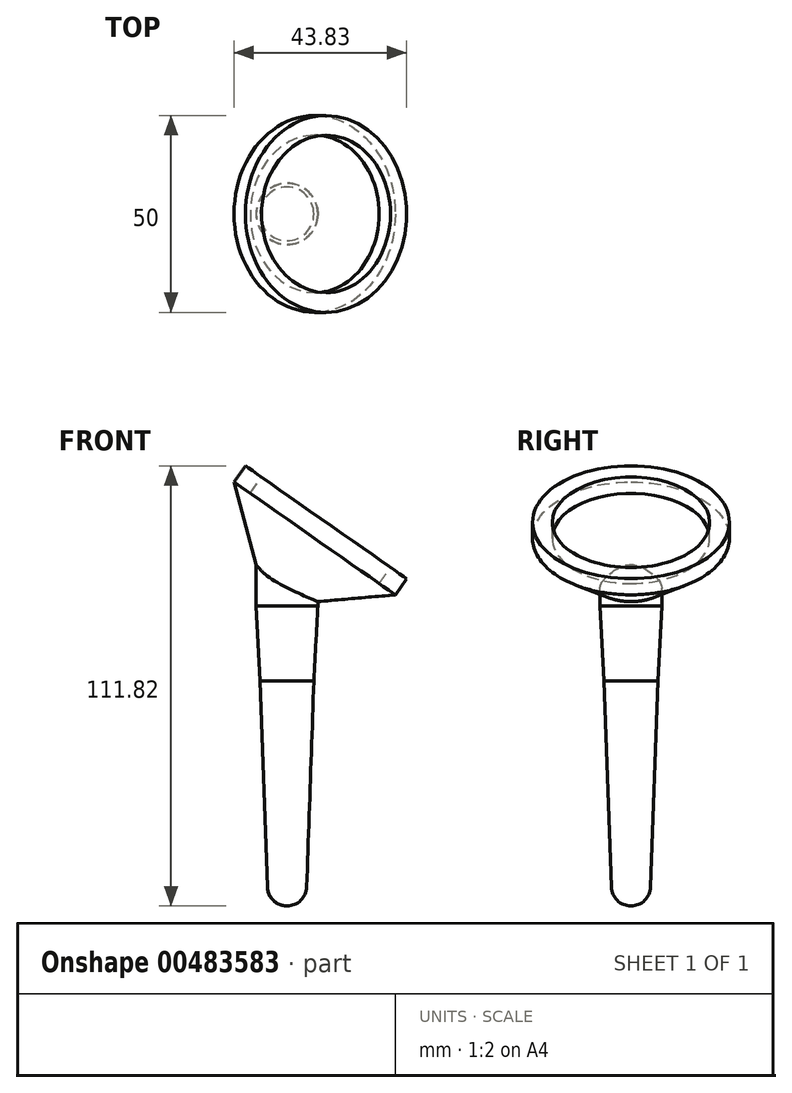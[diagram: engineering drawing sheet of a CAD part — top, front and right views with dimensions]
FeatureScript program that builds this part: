
annotation { "Feature Type Name" : "Feature", "Feature Type Description" : "" }
export const myFeature = defineFeature(function(context is Context, id is Id, definition is map)
    precondition{}
    {
        {
            var Q0;
            Q0=qCreatedBy(makeId("Front.planeOp"),FACE);
            var sketch = newSketch(context, id + "F0", { "sketchPlane" : qUnion([Q0])});
            skLineSegment(sketch, "E0", {"start": v(0, 84.87) * mm, "end": v(0, -76.2) * mm, "construction": true});
            skLineSegment(sketch, "E1", {"start": v(-7.82, 0) * mm, "end": v(0, 0) * mm, "construction": true});
            skCircle(sketch, "E2", {"center": v(0, -71.2) * mm, "radius": 5 * mm, "construction": true});
            skArc(sketch, "E3", {"start": v(-5, -71.37) * mm, "mid": v(-3.47, -74.8) * mm, "end": v(0, -76.2) * mm});
            skLineSegment(sketch, "E4", {"start": v(-5, -71.37) * mm, "end": v(-6.82, -19.05) * mm});
            skLineSegment(sketch, "E5", {"start": v(-6.82, -19.05) * mm, "end": v(-7.82, 0) * mm});
            skLineSegment(sketch, "E6", {"start": v(0, 0) * mm, "end": v(0, -76.2) * mm});
            skLineSegment(sketch, "E7", {"start": v(-7.82, 0) * mm, "end": v(-7.82, 20) * mm});
            skLineSegment(sketch, "E8", {"start": v(-7.82, 20) * mm, "end": v(0, 20) * mm});
            skLineSegment(sketch, "E9", {"start": v(0, 20) * mm, "end": v(0, 0) * mm});
            skSolve(sketch);
        }
        {
            var Q0;
            Q0 = qSketchRegion(id + "F0", true);
            var Q1;
            Q1=sQuery(id+"F0.wireOp",EDGE,"E0");
            revolve(context, id + "F1", {"entities" : qUnion([Q0]), "axis" : qUnion([Q1]), "revolveType" : RevolveType.FULL});
        }
        {
            var Q0;
            Q0=qCreatedBy(makeId("Top.planeOp"),FACE);
            var sketch = newSketch(context, id + "F2", { "sketchPlane" : qUnion([Q0])});
            skLineSegment(sketch, "E10", {"start": v(0, 0) * mm, "end": v(0, -167.53) * mm, "construction": true});
            skSolve(sketch);
        }
        {
            var Q0;
            Q0=qCreatedBy(makeId("Front.planeOp"),FACE);
            var sketch = newSketch(context, id + "F3", { "sketchPlane" : qUnion([Q0])});
            skLineSegment(sketch, "E11", {"start": v(-5, 0) * mm, "end": v(9.9, 21.28) * mm, "construction": true});
            skLineSegment(sketch, "E12", {"start": v(-5, 0) * mm, "end": v(-5, 23.33) * mm, "construction": true});
            skLineSegment(sketch, "E13", {"start": v(-5, 0) * mm, "end": v(27.51, 2.84) * mm});
            skLineSegment(sketch, "E14", {"start": v(27.51, 2.84) * mm, "end": v(30.38, 6.94) * mm});
            skLineSegment(sketch, "E15", {"start": v(30.38, 6.94) * mm, "end": v(9.9, 21.28) * mm});
            skLineSegment(sketch, "E16", {"start": v(-5, 0) * mm, "end": v(9.9, 21.28) * mm});
            skLineSegment(sketch, "E17", {"start": v(0, 0) * mm, "end": v(-5, 0) * mm});
            skSolve(sketch);
        }
        {
            var Q0;
            Q0=makeQuery(id+"F3.imprint","IMPRINT",FACE,{"disambiguationData":[TD([[makeQuery(id+"F3.imprint","IMPRINT",EDGE,{"derivedFrom":sQuery(id+"F3.wireOp",EDGE,"E13")}),1.0]])]});
            var Q1;
            Q1=sQuery(id+"F3.wireOp",EDGE,"E16");
            revolve(context, id + "F4", {"operationType" : NewBodyOperationType.ADD, "entities" : qUnion([Q0]), "axis" : qUnion([Q1]), "revolveType" : RevolveType.FULL});
        }
        {
            var Q0;
            Q0=makeQuery(id+"F4.opRevolve","SWEPT_FACE",FACE,{"disambiguationData":[OSD([sQuery(id+"F3.wireOp",EDGE,"E15")])]});
            var sketch = newSketch(context, id + "F5", { "sketchPlane" : qUnion([Q0])});
            skCircle(sketch, "E18", {"center": v(-4.1, 0) * mm, "radius": 20 * mm});
            skSolve(sketch);
        }
        {
            var Q0;
            Q0=makeQuery(id+"F5.imprint","IMPRINT",FACE,{"disambiguationData":[TD([[makeQuery(id+"F5.imprint","IMPRINT",EDGE,{"derivedFrom":sQuery(id+"F5.wireOp",EDGE,"E18")}),1.0]])]});
            extrude(context, id + "F6", {"entities" : qUnion([Q0]), "operationType" : NewBodyOperationType.REMOVE, "oppositeDirection" : true, "depth" : 5 * mm});
        }
    });
